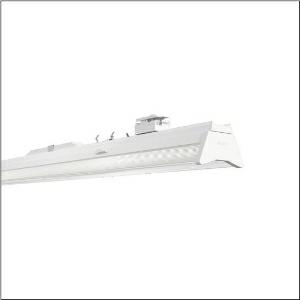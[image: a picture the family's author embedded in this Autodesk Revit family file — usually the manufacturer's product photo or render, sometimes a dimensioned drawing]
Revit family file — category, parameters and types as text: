
# Revit family: licross_r__21_performance_mo_52tm16cn49xg_ab5a
name_source: partatom
category: Lighting Fixtures
units: mm (PartAtom-declared; Revit-internal decimal feet)

## family parameters
Cut with Voids When Loaded = No
Host = Face
Light Source = No
Part Type = Normal
Room Calculation Point = No
Round Connector Dimension = Use Diameter
Shared = No

## types (1)
- --- (1 x LED, 9240 lm, 50.4 W, 4000K)
    Apparent Load = 50 VA
    CIE Flux Codes = 66 88 96 79 100
    Color Rendering = 80
    Color Temperature = 4000K
    Default Elevation = 1800 mm
    Description = Licross® 21 Performance MO, luminaire insert, of sheet steel, galvanised, coil coated, white, length: 1.500mm, width: 120mm, height: 123mm, LED rated luminous flux: 9.240lm, light colour: 840, control gear: ON/OFF Multilumen, CLOi, control gear: ECG Multilumen, with plug, 3-pole, with phase selection, mains connection: 220..240V, AC, 50/60Hz, start of lifetime: 50W, end of service life: 61W, halogen-free wiring, primary light control with lens, of plastic, primary optical cover: cover, of PMMA, light emission: direct/indirect distribution, primary light characteristic: symmetric, protection rating (complete): IP40, insulation class (complete): insulation class I (protective earthing), certification: CE, ENEC, UKCA, protection symbol: D if used in an environment without relevant dust loads with corresponding accessories, impact resistance: IK06, permissible ambient temperature for indoor applications: -35..+45°C, corresponds to IFS (International Featured Standards) requirements for safety and quality in the food industry, reducing of maximum allowable ambient temperature of 5°C with ceiling mounting, LABS conformity tested according to VDMA 24364:2018-05, packaging unit: 1 piece
    Height = 114 mm
    Lamp = 1 x LED
    Lamp Light Flux = 9240 lm
    Lamp Power = 50.4 W
    Lamp count = 1
    Length = 1500 mm
    Luminous efficacy = 183 lm/W
    Manufacturer = Siteco
    ModVariant = No
    Model = 52TM16CN49XG
    Mounting Place = Ceiling
    Mounting Type = Pendant
    Number of Poles = 1
    OnlyDefault = Yes
    Power Factor = 1
    Product Name = Licross® 21 Performance MO
    Product group = luminaire insert
    ProductGroupID = 902
    Protection Class = Protection class I
    Protection Degree = IP 40
    RLX_Detail_Level = 1
    RLX_Emergency_Light_Flux = 0 lm
    RLX_Emergency_Type = 0
    RLX_Emergency_Type_DB = No
    RlxData = <blob elided: 31813 chars, md5=26a9738f>
    Socket = socket
    Standby Power = 0 W
    System Light Flux = 9240 lm
    System Power = 50 W
    Type Comments = factory setting: luminous flux: 100 % | (A | C | E) | 117 mA
    Type Image = l_1256138.jpg
    URL = http://relux.com
    VarID = @adj_111598
    Voltage = 0 V
    Weight = 0.00 kg
    Width = 120 mm

## geometry (parser evidence)
native form markers: Blend x4, Sweep x11
no freeform markers — native parametric forms only
